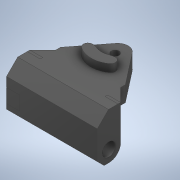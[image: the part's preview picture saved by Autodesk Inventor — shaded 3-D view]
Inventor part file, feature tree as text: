
AUTODESK INVENTOR PART (.ipt)
format: ipt  version: 2020 (Build 240168000, 168)  size: 280,064 bytes
history: native  units: in
note: dims shown in document units (in); Inventor stores cm internally (conversion verified against a paired STEP export)
features: extrude x6, sketch x6, projected_geometry x2, chamfer x1
ambient origin geometry x8: Origin, YZ Plane, XZ Plane, XY Plane, X Axis, Y Axis, Z Axis, Center Point
bodies: Solid2 (feature_tree), Solid1 (feature_tree)
feature tree (15):
  extrude  "add 5mm left side"  Depth=0.1969in TaperAngle=0.0deg
  extrude  "add 5 mm right side"  Depth=0.1969in
  chamfer  "support for 5mm extensions"  Distance=0.1969in
  extrude  "make bean smaller"  TaperAngle=45.0deg  [1 undecoded]
  extrude  "square off round for easy printing"  Depth=0.3937in TaperAngle=0.0deg
  extrude  "make standoff hole bigger"  Depth=0.126in TaperAngle=0.0deg
  extrude  "make bottom plate space bigger"  [1 undecoded]
  sketch  "Sketch1"  dims[d0=0.1969in d1=0.0in d7=0.1969in d8=0.0in]
  sketch  "Sketch2"  dims[d9=0.1969in d10=0.0787in d11=45.0deg d12=0.0039in d13=0.1969in d14=0.0in]
  sketch  "Sketch3"  dims[d15=0.3937in d16=0.0in d18=45.0deg]
  projected_geometry  "Projected Loop1"
  sketch  "Sketch4"  dims[d19=0.2008in d20=0.3937in d21=0.0in]
  projected_geometry  "Projected Loop2"
  sketch  "Sketch5"  dims[d22=0.0118in d23=0.126in d24=0.0in]
  sketch  "Sketch6"
note: 2 required parameter values undecoded (feature->parameter linkage not recoverable at this tier; creation-order binding heuristic only, values carry confidence <= 0.55)
